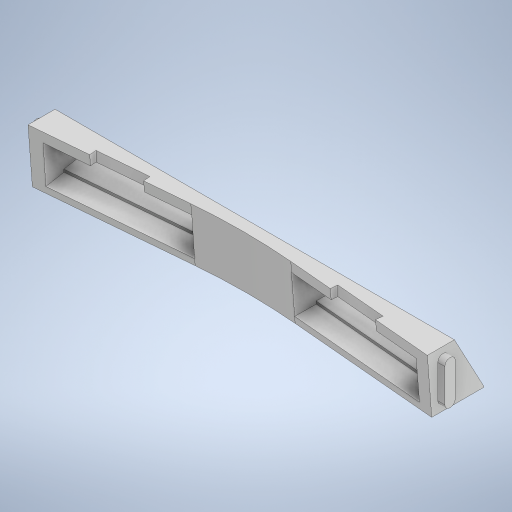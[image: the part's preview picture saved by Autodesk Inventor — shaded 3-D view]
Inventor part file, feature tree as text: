
AUTODESK INVENTOR PART (.ipt)
format: ipt  version: 2023 (Build 270158000, 158)  size: 508,928 bytes
history: native  units: mm
features: projected_geometry x18, extrude x16, sketch x16, other x14, reference x4, fillet x2, mirror x1
ambient origin geometry x8: Origin, YZ Plane, XZ Plane, XY Plane, X Axis, Y Axis, Z Axis, Center Point
bodies: Body1 (feature_tree)
feature tree (71):
  other  "Bryła1"
  extrude  "Wyciągnięcie proste1"  Depth=10.796607mm
  extrude  "Wyciągnięcie proste2"  Depth=10.0mm
  extrude  "Wyciągnięcie proste3"  Depth=2.5mm
  extrude  "Wyciągnięcie proste4"  Depth=25.0mm TaperAngle=0.0deg
  other  "Edytuj bezpośrednio1"
  extrude  "Wyciągnięcie proste7"  Depth=14.835299mm
  extrude  "Wyciągnięcie proste8"  Depth=14.835299mm
  extrude  "Wyciągnięcie proste9"  TaperAngle=0.0deg  [1 undecoded]
  extrude  "Wyciągnięcie proste10"  Depth=1.0mm TaperAngle=0.0deg
  sketch  "Szkic11"
  other  "Płaszczyzna konstrukcyjna1"
  extrude  "Wyciągnięcie proste11"  Depth=1.0mm TaperAngle=0.0deg
  extrude  "Wyciągnięcie proste12"  Depth=2.0mm TaperAngle=0.0deg
  extrude  "Wyciągnięcie proste13"  Depth=6.3mm
  extrude  "Wyciągnięcie proste14"  Depth=8.4mm
  extrude  "Wyciągnięcie proste15"  Depth=0.774926mm
  mirror  "Odbij3"
  other  "Edytuj bezpośrednio7"
  other  "Edytuj bezpośrednio8"
  extrude  "Wyciągnięcie proste16"  Depth=29.5mm TaperAngle=0.0deg
  extrude  "Wyciągnięcie proste17"  Depth=2.0mm TaperAngle=0.0deg
  extrude  "Wyciągnięcie proste18"  Depth=0.6mm TaperAngle=0.0deg
  fillet  "Zaokrąglenie1"  [1 undecoded]
  fillet  "Zaokrąglenie2"  Radius=0.3mm
  sketch  "Szkic1"
  sketch  "Szkic2"
  projected_geometry  "Pętla rzutowana1"
  projected_geometry  "Pętla rzutowana2"
  sketch  "Szkic3"
  projected_geometry  "Pętla rzutowana3"
  sketch  "Szkic4"
  projected_geometry  "Pętla rzutowana4"
  sketch  "Szkic7"
  sketch  "Szkic8"
  projected_geometry  "Pętla rzutowana7"
  projected_geometry  "Pętla rzutowana8"
  sketch  "Szkic9"
  projected_geometry  "Pętla rzutowana9"
  reference  "Odniesienie1"
  sketch  "Szkic10"
  projected_geometry  "Pętla rzutowana10"
  projected_geometry  "Pętla rzutowana11"
  reference  "Odniesienie2"
  reference  "Odniesienie3"
  sketch  "Szkic14"
  projected_geometry  "Pętla rzutowana14"
  sketch  "Szkic15"
  projected_geometry  "Pętla rzutowana15"
  projected_geometry  "Pętla rzutowana16"
  sketch  "Szkic16"
  projected_geometry  "Pętla rzutowana17"
  sketch  "Szkic17"
  projected_geometry  "Pętla rzutowana18"
  sketch  "Szkic18"
  projected_geometry  "Pętla rzutowana19"
  projected_geometry  "Pętla rzutowana20"
  reference  "Odniesienie4"
  sketch  "Szkic19"
  projected_geometry  "Pętla rzutowana21"
  sketch  "Szkic20"
  projected_geometry  "Pętla rzutowana22"
  other  "Przesuń1"
  other  "<userpath>\Desktop\MojeRoboty\Stefan\mechanics 2\STEFAN.iam"
  other  "STEFAN.iam"
  other  "GP2Y0A41SK0F:2"
  other  "Przesuń8"
  other  "Przesuń9"
  other  "Przesuń10"
  other  "Przesuń11"
  other  "sciana_awaryjna:1"
note: 2 required parameter values undecoded (feature->parameter linkage not recoverable at this tier; creation-order binding heuristic only, values carry confidence <= 0.55)
